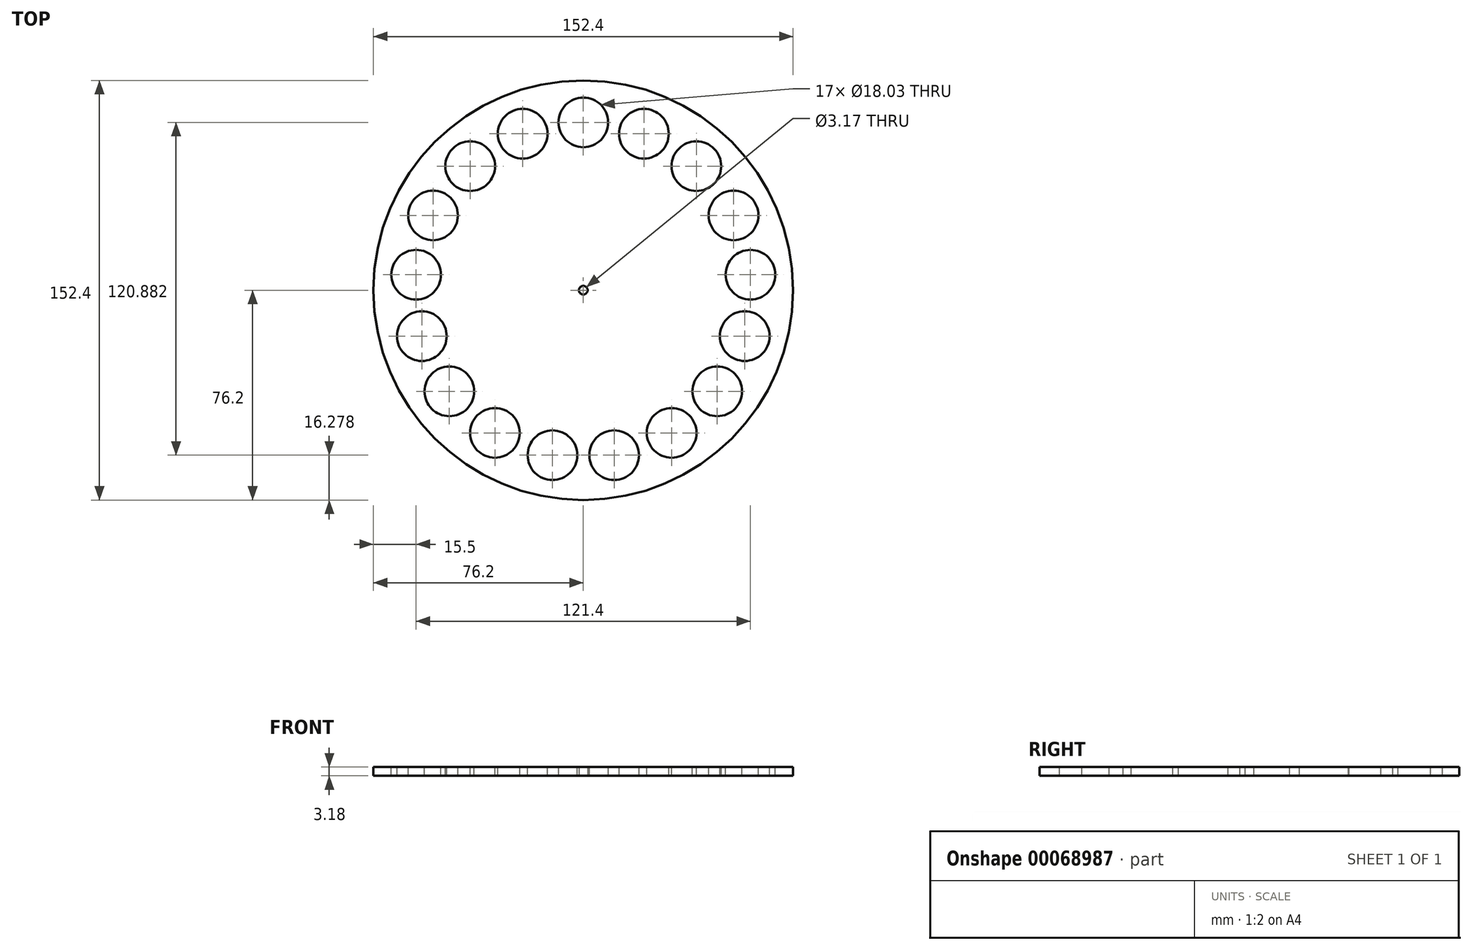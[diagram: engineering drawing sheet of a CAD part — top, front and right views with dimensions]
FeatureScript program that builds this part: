
annotation { "Feature Type Name" : "Feature", "Feature Type Description" : "" }
export const myFeature = defineFeature(function(context is Context, id is Id, definition is map)
    precondition{}
    {
        {
            var Q0;
            Q0=qCreatedBy(makeId("Top.planeOp"),FACE);
            var sketch = newSketch(context, id + "F0", { "sketchPlane" : qUnion([Q0])});
            skCircle(sketch, "E0", {"center": v(0, 0) * mm, "radius": 76.2 * mm});
            skCircle(sketch, "E1", {"center": v(0, 0) * mm, "radius": 1.59 * mm});
            skLineSegment(sketch, "E2", {"start": v(0, 0) * mm, "end": v(0, 76.2) * mm});
            skCircle(sketch, "E3", {"center": v(0, 60.96) * mm, "radius": 9.02 * mm});
            skSolve(sketch);
        }
        {
            var Q0;
            {var subQ0=sQuery(id+"F0.wireOp",EDGE,"E3");var subQ1=sQuery(id+"F0.wireOp",EDGE,"E2");var subQ2=makeQuery(id+"F0.imprint","INTERSECT",VERTEX,{"disambiguationData":[OD(0.0)],"derivedFrom":[subQ1,subQ0]});Q0=makeQuery(id+"F0.imprint","IMPRINT",FACE,{"disambiguationData":[TD([[makeQuery(id+"F0.imprint","IMPRINT",EDGE,{"disambiguationData":[TD([[subQ2,-1.0]])],"derivedFrom":subQ1}),-1.0]])]});}
            var Q1;
            {var subQ0=sQuery(id+"F0.wireOp",EDGE,"E3");var subQ1=sQuery(id+"F0.wireOp",EDGE,"E2");var subQ2=makeQuery(id+"F0.imprint","INTERSECT",VERTEX,{"disambiguationData":[OD(0.0)],"derivedFrom":[subQ1,subQ0]});Q1=makeQuery(id+"F0.imprint","IMPRINT",FACE,{"disambiguationData":[TD([[makeQuery(id+"F0.imprint","IMPRINT",EDGE,{"disambiguationData":[TD([[subQ2,-1.0]])],"derivedFrom":subQ1}),1.0]])]});}
            extrude(context, id + "F1", {"entities" : qUnion([Q0, Q1]), "depth" : 25.4 * mm});
        }
        {
            var Q0;
            Q0 = qSketchRegion(id + "F0", true);
            extrude(context, id + "F2", {"entities" : qUnion([Q0]), "depth" : 3.17 * mm});
        }
        {
            var Q0;
            Q0=makeQuery(id+"F1.opExtrude","SWEPT_BODY",BODY,{"disambiguationData":[OSD([sQuery(id+"F0.wireOp",EDGE,"E3")])]});
            var Q1;
            Q1=makeQuery(id+"F2.opExtrude","CAP_EDGE",EDGE,{"disambiguationData":[OSD([sQuery(id+"F0.wireOp",EDGE,"E0")])],"isStart":false});
            circularPattern(context, id + "F3", {"entities" : qUnion([Q0]), "axis" : qUnion([Q1]), "angle" : 360 * degree, "instanceCount" : 17, "equalSpace" : true});
        }
        {
            var Q0;
            Q0=makeQuery(id+"F1.opExtrude","CAP_FACE",FACE,{"disambiguationData":[OSD([sQuery(id+"F0.wireOp",EDGE,"E3")])],"isStart":false});
            var Q1;
            Q1=makeQuery(id+"F3.opPattern","COPY",FACE,{"derivedFrom":makeQuery(id+"F1.opExtrude","CAP_FACE",FACE,{"disambiguationData":[OSD([sQuery(id+"F0.wireOp",EDGE,"E3")])],"isStart":false}),"instanceName":"1"});
            var Q2;
            Q2=makeQuery(id+"F3.opPattern","COPY",FACE,{"derivedFrom":makeQuery(id+"F1.opExtrude","CAP_FACE",FACE,{"disambiguationData":[OSD([sQuery(id+"F0.wireOp",EDGE,"E3")])],"isStart":false}),"instanceName":"2"});
            var Q3;
            Q3=makeQuery(id+"F3.opPattern","COPY",FACE,{"derivedFrom":makeQuery(id+"F1.opExtrude","CAP_FACE",FACE,{"disambiguationData":[OSD([sQuery(id+"F0.wireOp",EDGE,"E3")])],"isStart":false}),"instanceName":"3"});
            var Q4;
            Q4=makeQuery(id+"F3.opPattern","COPY",FACE,{"derivedFrom":makeQuery(id+"F1.opExtrude","CAP_FACE",FACE,{"disambiguationData":[OSD([sQuery(id+"F0.wireOp",EDGE,"E3")])],"isStart":false}),"instanceName":"4"});
            var Q5;
            Q5=makeQuery(id+"F3.opPattern","COPY",FACE,{"derivedFrom":makeQuery(id+"F1.opExtrude","CAP_FACE",FACE,{"disambiguationData":[OSD([sQuery(id+"F0.wireOp",EDGE,"E3")])],"isStart":false}),"instanceName":"5"});
            var Q6;
            Q6=makeQuery(id+"F3.opPattern","COPY",FACE,{"derivedFrom":makeQuery(id+"F1.opExtrude","CAP_FACE",FACE,{"disambiguationData":[OSD([sQuery(id+"F0.wireOp",EDGE,"E3")])],"isStart":false}),"instanceName":"6"});
            var Q7;
            Q7=makeQuery(id+"F3.opPattern","COPY",FACE,{"derivedFrom":makeQuery(id+"F1.opExtrude","CAP_FACE",FACE,{"disambiguationData":[OSD([sQuery(id+"F0.wireOp",EDGE,"E3")])],"isStart":false}),"instanceName":"7"});
            var Q8;
            Q8=makeQuery(id+"F3.opPattern","COPY",FACE,{"derivedFrom":makeQuery(id+"F1.opExtrude","CAP_FACE",FACE,{"disambiguationData":[OSD([sQuery(id+"F0.wireOp",EDGE,"E3")])],"isStart":false}),"instanceName":"8"});
            var Q9;
            Q9=makeQuery(id+"F3.opPattern","COPY",FACE,{"derivedFrom":makeQuery(id+"F1.opExtrude","CAP_FACE",FACE,{"disambiguationData":[OSD([sQuery(id+"F0.wireOp",EDGE,"E3")])],"isStart":false}),"instanceName":"9"});
            var Q10;
            Q10=makeQuery(id+"F3.opPattern","COPY",FACE,{"derivedFrom":makeQuery(id+"F1.opExtrude","CAP_FACE",FACE,{"disambiguationData":[OSD([sQuery(id+"F0.wireOp",EDGE,"E3")])],"isStart":false}),"instanceName":"19"});
            var Q11;
            Q11=makeQuery(id+"F3.opPattern","COPY",FACE,{"derivedFrom":makeQuery(id+"F1.opExtrude","CAP_FACE",FACE,{"disambiguationData":[OSD([sQuery(id+"F0.wireOp",EDGE,"E3")])],"isStart":false}),"instanceName":"18"});
            var Q12;
            Q12=makeQuery(id+"F3.opPattern","COPY",FACE,{"derivedFrom":makeQuery(id+"F1.opExtrude","CAP_FACE",FACE,{"disambiguationData":[OSD([sQuery(id+"F0.wireOp",EDGE,"E3")])],"isStart":false}),"instanceName":"17"});
            var Q13;
            Q13=makeQuery(id+"F3.opPattern","COPY",FACE,{"derivedFrom":makeQuery(id+"F1.opExtrude","CAP_FACE",FACE,{"disambiguationData":[OSD([sQuery(id+"F0.wireOp",EDGE,"E3")])],"isStart":false}),"instanceName":"16"});
            var Q14;
            Q14=makeQuery(id+"F3.opPattern","COPY",FACE,{"derivedFrom":makeQuery(id+"F1.opExtrude","CAP_FACE",FACE,{"disambiguationData":[OSD([sQuery(id+"F0.wireOp",EDGE,"E3")])],"isStart":false}),"instanceName":"15"});
            var Q15;
            Q15=makeQuery(id+"F3.opPattern","COPY",FACE,{"derivedFrom":makeQuery(id+"F1.opExtrude","CAP_FACE",FACE,{"disambiguationData":[OSD([sQuery(id+"F0.wireOp",EDGE,"E3")])],"isStart":false}),"instanceName":"14"});
            var Q16;
            Q16=makeQuery(id+"F3.opPattern","COPY",FACE,{"derivedFrom":makeQuery(id+"F1.opExtrude","CAP_FACE",FACE,{"disambiguationData":[OSD([sQuery(id+"F0.wireOp",EDGE,"E3")])],"isStart":false}),"instanceName":"12"});
            var Q17;
            Q17=makeQuery(id+"F3.opPattern","COPY",FACE,{"derivedFrom":makeQuery(id+"F1.opExtrude","CAP_FACE",FACE,{"disambiguationData":[OSD([sQuery(id+"F0.wireOp",EDGE,"E3")])],"isStart":false}),"instanceName":"11"});
            var Q18;
            Q18=makeQuery(id+"F3.opPattern","COPY",FACE,{"derivedFrom":makeQuery(id+"F1.opExtrude","CAP_FACE",FACE,{"disambiguationData":[OSD([sQuery(id+"F0.wireOp",EDGE,"E3")])],"isStart":false}),"instanceName":"10"});
            var Q19;
            Q19=makeQuery(id+"F3.opPattern","COPY",FACE,{"derivedFrom":makeQuery(id+"F1.opExtrude","CAP_FACE",FACE,{"disambiguationData":[OSD([sQuery(id+"F0.wireOp",EDGE,"E3")])],"isStart":false}),"instanceName":"13"});
            extrude(context, id + "F4", {"entities" : qUnion([Q0, Q1, Q2, Q3, Q4, Q5, Q6, Q7, Q8, Q9, Q10, Q11, Q12, Q13, Q14, Q15, Q16, Q17, Q18, Q19]), "operationType" : NewBodyOperationType.REMOVE, "oppositeDirection" : true, "depth" : 25.4 * mm});
        }
    });
